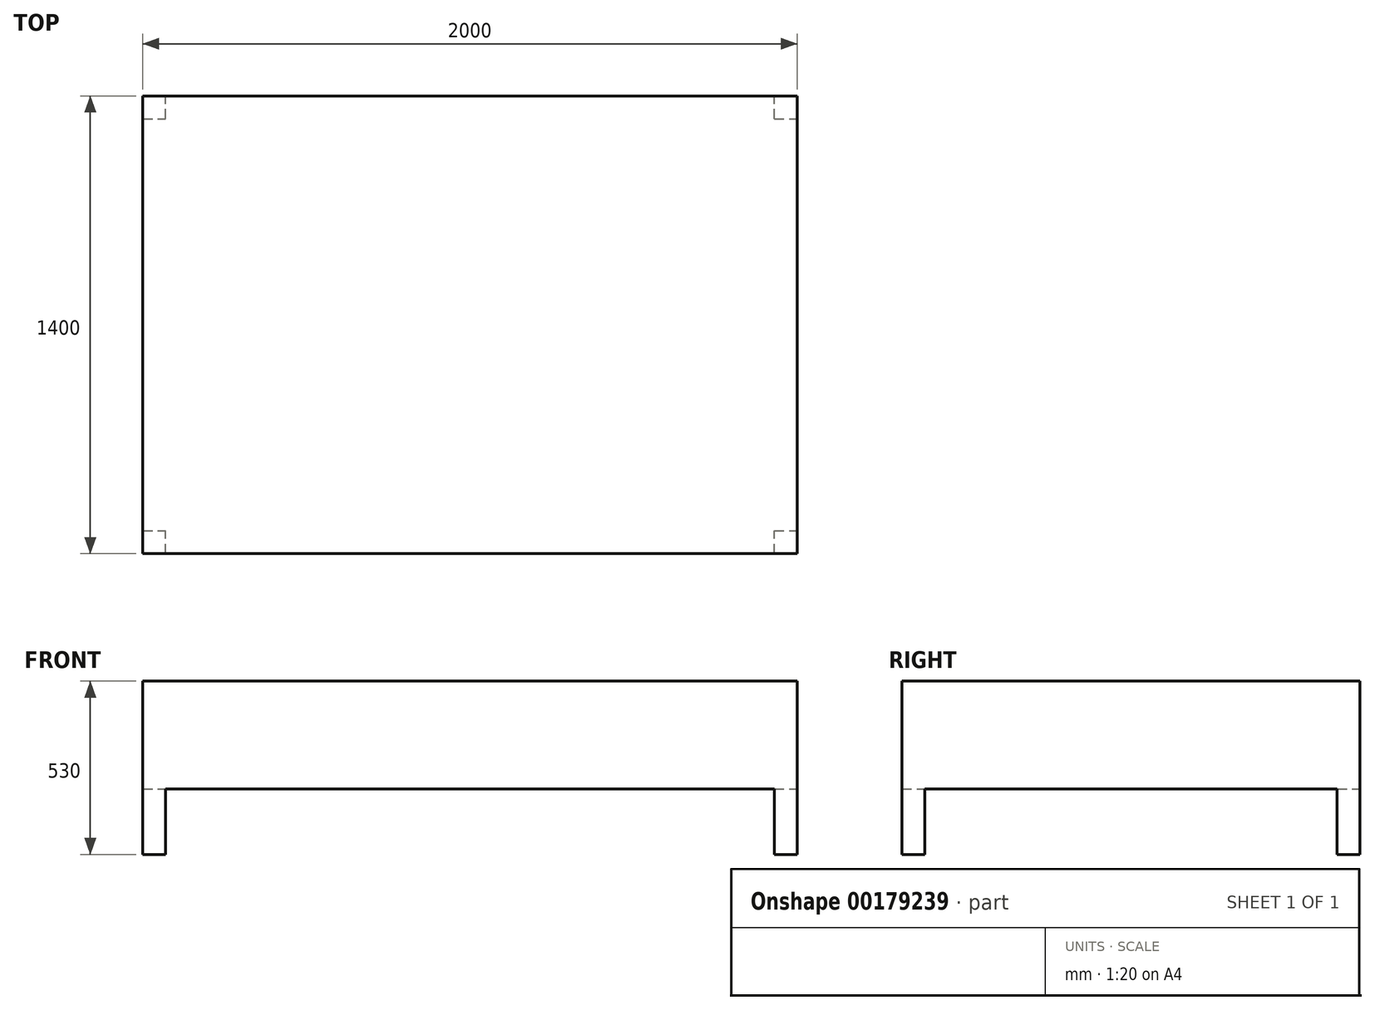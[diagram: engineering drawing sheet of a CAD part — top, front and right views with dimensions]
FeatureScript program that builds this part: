
annotation { "Feature Type Name" : "Feature", "Feature Type Description" : "" }
export const myFeature = defineFeature(function(context is Context, id is Id, definition is map)
    precondition{}
    {
        {
            var Q0;
            Q0=qCreatedBy(makeId("Top.planeOp"),FACE);
            cPlane(context, id + "F0", {"entities" : qUnion([Q0]), "cplaneType" : CPlaneType.OFFSET, "offset" : 200 * mm, "width" : 150 * mm, "height" : 150 * mm});
        }
        {
            var Q0;
            Q0=qCreatedBy(makeId("Top.planeOp"),FACE);
            cPlane(context, id + "F1", {"entities" : qUnion([Q0]), "cplaneType" : CPlaneType.OFFSET, "offset" : 530 * mm, "width" : 150 * mm, "height" : 150 * mm});
        }
        {
            var Q0;
            Q0=qCreatedBy(id+"F0.planeOp",FACE);
            var sketch = newSketch(context, id + "F2", { "sketchPlane" : qUnion([Q0])});
            skLineSegment(sketch, "E0.bottom", {"start": v(0, 0) * mm, "end": v(2000, 0) * mm});
            skLineSegment(sketch, "E0.top", {"start": v(0, 1400) * mm, "end": v(2000, 1400) * mm});
            skLineSegment(sketch, "E0.left", {"start": v(0, 0) * mm, "end": v(0, 1400) * mm});
            skLineSegment(sketch, "E0.right", {"start": v(2000, 0) * mm, "end": v(2000, 1400) * mm});
            skSolve(sketch);
        }
        {
            var Q0;
            Q0 = qSketchRegion(id + "F2", true);
            var Q1;
            Q1=qCreatedBy(id+"F1.planeOp",FACE);
            extrude(context, id + "F3", {"entities" : qUnion([Q0]), "endBound" : BoundingType.UP_TO_SURFACE, "endBoundEntityFace" : qUnion([Q1]), "depth" : 25 * mm});
        }
        {
            var Q0;
            Q0=qCreatedBy(makeId("Top.planeOp"),FACE);
            var sketch = newSketch(context, id + "F4", { "sketchPlane" : qUnion([Q0])});
            skLineSegment(sketch, "E1.bottom", {"start": v(0, 0) * mm, "end": v(70, 0) * mm});
            skLineSegment(sketch, "E1.top", {"start": v(0, 70) * mm, "end": v(70, 70) * mm});
            skLineSegment(sketch, "E1.left", {"start": v(0, 0) * mm, "end": v(0, 70) * mm});
            skLineSegment(sketch, "E1.right", {"start": v(70, 0) * mm, "end": v(70, 70) * mm});
            skLineSegment(sketch, "E2.0.1.0", {"start": v(0, 1330) * mm, "end": v(70, 1330) * mm});
            skLineSegment(sketch, "E2.0.1.1", {"start": v(0, 1400) * mm, "end": v(70, 1400) * mm});
            skLineSegment(sketch, "E2.0.1.2", {"start": v(0, 1330) * mm, "end": v(0, 1400) * mm});
            skLineSegment(sketch, "E2.0.1.3", {"start": v(70, 1330) * mm, "end": v(70, 1400) * mm});
            skLineSegment(sketch, "E2.1.0.0", {"start": v(1930, 0) * mm, "end": v(2000, 0) * mm});
            skLineSegment(sketch, "E2.1.0.1", {"start": v(1930, 70) * mm, "end": v(2000, 70) * mm});
            skLineSegment(sketch, "E2.1.0.2", {"start": v(1930, 0) * mm, "end": v(1930, 70) * mm});
            skLineSegment(sketch, "E2.1.0.3", {"start": v(2000, 0) * mm, "end": v(2000, 70) * mm});
            skLineSegment(sketch, "E2.1.1.0", {"start": v(1930, 1330) * mm, "end": v(2000, 1330) * mm});
            skLineSegment(sketch, "E2.1.1.1", {"start": v(1930, 1400) * mm, "end": v(2000, 1400) * mm});
            skLineSegment(sketch, "E2.1.1.2", {"start": v(1930, 1330) * mm, "end": v(1930, 1400) * mm});
            skLineSegment(sketch, "E2.1.1.3", {"start": v(2000, 1330) * mm, "end": v(2000, 1400) * mm});
            skLineSegment(sketch, "E2.direction1", {"start": v(0, 0) * mm, "end": v(1930, 0) * mm, "construction": true});
            skLineSegment(sketch, "E2.direction2", {"start": v(0, 0) * mm, "end": v(0, 1330) * mm, "construction": true});
            skSolve(sketch);
        }
        {
            var Q0;
            Q0=makeQuery(id+"F4.imprint","IMPRINT",FACE,{"disambiguationData":[TD([[makeQuery(id+"F4.imprint","IMPRINT",EDGE,{"derivedFrom":sQuery(id+"F4.wireOp",EDGE,"E1.bottom")}),1.0]])]});
            var Q1;
            Q1=makeQuery(id+"F4.imprint","IMPRINT",FACE,{"disambiguationData":[TD([[makeQuery(id+"F4.imprint","IMPRINT",EDGE,{"derivedFrom":sQuery(id+"F4.wireOp",EDGE,"E2.1.0.0")}),1.0]])]});
            var Q2;
            Q2=makeQuery(id+"F4.imprint","IMPRINT",FACE,{"disambiguationData":[TD([[makeQuery(id+"F4.imprint","IMPRINT",EDGE,{"derivedFrom":sQuery(id+"F4.wireOp",EDGE,"E2.1.1.0")}),1.0]])]});
            var Q3;
            Q3=makeQuery(id+"F4.imprint","IMPRINT",FACE,{"disambiguationData":[TD([[makeQuery(id+"F4.imprint","IMPRINT",EDGE,{"derivedFrom":sQuery(id+"F4.wireOp",EDGE,"E2.0.1.0")}),1.0]])]});
            var Q4;
            Q4=makeQuery(id+"F3.opExtrude","CAP_FACE",FACE,{"disambiguationData":[OSD([sQuery(id+"F2.wireOp",EDGE,"E0.bottom"),sQuery(id+"F2.wireOp",EDGE,"E0.top"),sQuery(id+"F2.wireOp",EDGE,"E0.left"),sQuery(id+"F2.wireOp",EDGE,"E0.right")])],"isStart":true});
            extrude(context, id + "F5", {"entities" : qUnion([Q0, Q1, Q2, Q3]), "operationType" : NewBodyOperationType.ADD, "endBound" : BoundingType.UP_TO_SURFACE, "endBoundEntityFace" : qUnion([Q4]), "depth" : 25 * mm});
        }
    });
